# Revit family: BENCH_PRIMARYPLUS_4P
name_source: partatom
category: Furniture
units: mm (PartAtom-declared; Revit-internal decimal feet)

## family parameters
Always vertical = Yes
Cut with Voids When Loaded = No
OmniClass Number = 23.40.20.00
OmniClass Title = General Furniture and Specialties
Room Calculation Point = No
Shared = No
Work Plane-Based = No

## types (24) — shared parameters
ADDITIONAL = No
CUTOUT_WT = No
FULL_WT = Yes
Manufacturer = IBR InnovaSystem
URL = https://ibr-innovasystem.com
WT_12-75_XL = No
WT_15-75_XL = No
WT_6-75_XL = No
WT_9-75_XL = No
XL_WORKTOP = No
midleg = No
zero-valued in all types: Default Elevation

## per-type parameters (varying)
| type | Description | HEIGHT | LOW_TAG | Length | WT_12-75 | WT_15-75 | WT_6-75 | WT_9-75 | depth |
| PRBP-15759 | Primary Bench Plus 1500x750x900 Fixed Shelf 150mm deep, 3 Sockets at right column. | 900 mm  [stored 2.95276 ft] | No | 1500 mm  [stored 4.92126 ft] | No | Yes | No | No | 750 mm  [stored 2.46063 ft] |
| PRBP-15909 | Primary Bench Plus 1500x900x900 Fixed Shelf 150mm deep, 3 Sockets at right column. | 900 mm  [stored 2.95276 ft] | No | 1500 mm  [stored 4.92126 ft] | No | Yes | No | No | 900 mm  [stored 2.95276 ft] |
| PRBP-15609 | Primary Bench Plus 1500x600x900 Fixed Shelf 150mm deep, 3 Sockets at right column. | 900 mm  [stored 2.95276 ft] | No | 1500 mm  [stored 4.92126 ft] | No | Yes | No | No | 600 mm  [stored 1.9685 ft] |
| PRBP-15757 | Primary Bench Plus 1500x750x750 Fixed Shelf 150mm deep, 3 Sockets at right column. | 750 mm  [stored 2.46063 ft] | Yes | 1500 mm  [stored 4.92126 ft] | No | Yes | No | No | 750 mm  [stored 2.46063 ft] |
| PRBP-15907 | Primary Bench Plus 1500x900x750 Fixed Shelf 150mm deep, 3 Sockets at right column. | 750 mm  [stored 2.46063 ft] | Yes | 1500 mm  [stored 4.92126 ft] | No | Yes | No | No | 900 mm  [stored 2.95276 ft] |
| PRBP-15607 | Primary Bench Plus 1500x600x750 Fixed Shelf 150mm deep, 3 Sockets at right column. | 750 mm  [stored 2.46063 ft] | Yes | 1500 mm  [stored 4.92126 ft] | No | Yes | No | No | 600 mm  [stored 1.9685 ft] |
| PRBP-12759 | Primary Bench Plus 1200x750x900 Fixed Shelf 150mm deep, 3 Sockets at right column. | 900 mm  [stored 2.95276 ft] | No | 1200 mm | Yes | No | No | No | 750 mm  [stored 2.46063 ft] |
| PRBP-12909 | Primary Bench Plus 1200x900x900 Fixed Shelf 150mm deep, 3 Sockets at right column. | 900 mm  [stored 2.95276 ft] | No | 1200 mm | Yes | No | No | No | 900 mm  [stored 2.95276 ft] |
| PRBP-12609 | Primary Bench Plus 1200x600x900 Fixed Shelf 150mm deep, 3 Sockets at right column. | 900 mm  [stored 2.95276 ft] | No | 1200 mm | Yes | No | No | No | 600 mm  [stored 1.9685 ft] |
| PRBP-12757 | Primary Bench Plus 1200x750x750 Fixed Shelf 150mm deep, 3 Sockets at right column. | 750 mm  [stored 2.46063 ft] | Yes | 1200 mm | Yes | No | No | No | 750 mm  [stored 2.46063 ft] |
| PRBP-12907 | Primary Bench Plus 1200x900x750 Fixed Shelf 150mm deep, 3 Sockets at right column. | 750 mm  [stored 2.46063 ft] | Yes | 1200 mm | Yes | No | No | No | 900 mm  [stored 2.95276 ft] |
| PRBP-12607 | Primary Bench Plus 1200x600x750 Fixed Shelf 150mm deep, 3 Sockets at right column. | 750 mm  [stored 2.46063 ft] | Yes | 1200 mm | Yes | No | No | No | 600 mm  [stored 1.9685 ft] |
| PRBP-09759 | Primary Bench Plus 900x750x900 Fixed Shelf 150mm deep, 3 Sockets at right column. | 900 mm  [stored 2.95276 ft] | No | 900 mm  [stored 2.95276 ft] | No | No | No | Yes | 750 mm  [stored 2.46063 ft] |
| PRBP-09909 | Primary Bench Plus 900x900x900 Fixed Shelf 150mm deep, 3 Sockets at right column. | 900 mm  [stored 2.95276 ft] | No | 900 mm  [stored 2.95276 ft] | No | No | No | Yes | 900 mm  [stored 2.95276 ft] |
| PRBP-09609 | Primary Bench Plus 900x600x900 Fixed Shelf 150mm deep, 3 Sockets at right column. | 900 mm  [stored 2.95276 ft] | No | 900 mm  [stored 2.95276 ft] | No | No | No | Yes | 600 mm  [stored 1.9685 ft] |
| PRBP-09757 | Primary Bench Plus 900x750x750 Fixed Shelf 150mm deep, 3 Sockets at right column. | 750 mm  [stored 2.46063 ft] | Yes | 900 mm  [stored 2.95276 ft] | No | No | No | Yes | 750 mm  [stored 2.46063 ft] |
| PRBP-09907 | Primary Bench Plus 900x900x750 Fixed Shelf 150mm deep, 3 Sockets at right column. | 750 mm  [stored 2.46063 ft] | Yes | 900 mm  [stored 2.95276 ft] | No | No | No | Yes | 900 mm  [stored 2.95276 ft] |
| PRBP-09607 | Primary Bench Plus 900x600x750 Fixed Shelf 150mm deep, 3 Sockets at right column. | 750 mm  [stored 2.46063 ft] | Yes | 900 mm  [stored 2.95276 ft] | No | No | No | Yes | 600 mm  [stored 1.9685 ft] |
| PRBP-06759 | Primary Bench Plus 600x750x900 Fixed Shelf 150mm deep, 3 Sockets at right column. | 900 mm  [stored 2.95276 ft] | No | 600 mm  [stored 1.9685 ft] | No | No | Yes | No | 750 mm  [stored 2.46063 ft] |
| PRBP-06909 | Primary Bench Plus 600x900x900 Fixed Shelf 150mm deep, 3 Sockets at right column. | 900 mm  [stored 2.95276 ft] | No | 600 mm  [stored 1.9685 ft] | No | No | Yes | No | 900 mm  [stored 2.95276 ft] |
| PRBP-06609 | Primary Bench Plus 600x600x900 Fixed Shelf 150mm deep, 3 Sockets at right column. | 900 mm  [stored 2.95276 ft] | No | 600 mm  [stored 1.9685 ft] | No | No | Yes | No | 600 mm  [stored 1.9685 ft] |
| PRBP-06757 | Primary Bench Plus 600x750x750 Fixed Shelf 150mm deep, 3 Sockets at right column. | 750 mm  [stored 2.46063 ft] | Yes | 600 mm  [stored 1.9685 ft] | No | No | Yes | No | 750 mm  [stored 2.46063 ft] |
| PRBP-06907 | Primary Bench Plus 600x900x750 Fixed Shelf 150mm deep, 3 Sockets at right column. | 750 mm  [stored 2.46063 ft] | Yes | 600 mm  [stored 1.9685 ft] | No | No | Yes | No | 900 mm  [stored 2.95276 ft] |
| PRBP-06607 | Primary Bench Plus 600x600x750, Fixed Shelf 150mm deep, 3 Sockets at right column. | 750 mm  [stored 2.46063 ft] | Yes | 600 mm  [stored 1.9685 ft] | No | No | Yes | No | 600 mm  [stored 1.9685 ft] |

note: [stored X ft] marks values corroborated as IEEE doubles in the binary element streams (Revit-internal decimal feet)

## geometry (parser evidence)
native form markers: Sweep x29
no freeform markers — native parametric forms only
